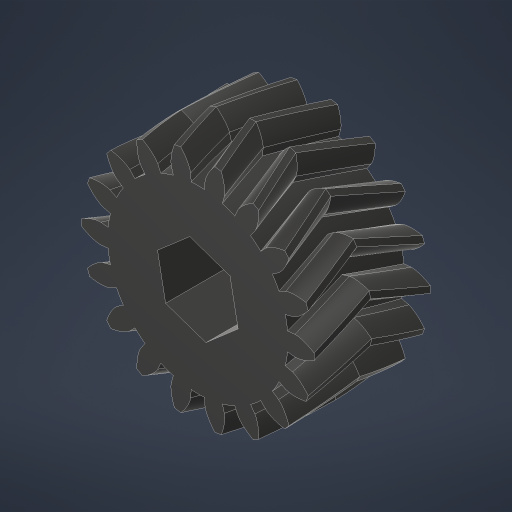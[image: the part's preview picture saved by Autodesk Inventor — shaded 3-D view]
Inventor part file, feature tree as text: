
AUTODESK INVENTOR PART (.ipt)
format: ipt  version: 2023.4 (Build 274418000, 418)  size: 706,048 bytes
history: native  units: in
note: dims shown in document units (in); Inventor stores cm internally (conversion verified against a paired STEP export)
features: other x2, extrude x1, sketch x1
ambient origin geometry x8: Origin, YZ Plane, XZ Plane, XY Plane, X Axis, Y Axis, Z Axis, Center Point
bodies: Solid1 (feature_tree)
feature tree (4):
  extrude  "Extrusion1"  TaperAngle=0.0deg  [1 undecoded]
  other  "DIAMETRIC PITCH"
  sketch  "Sketch1"  dims[d0=0.5in d1=0.0in d2=0.0in d3=1.4173in]
  other  "Helical 2M 18T"
note: 1 required parameter value undecoded (feature->parameter linkage not recoverable at this tier; creation-order binding heuristic only, values carry confidence <= 0.55)
